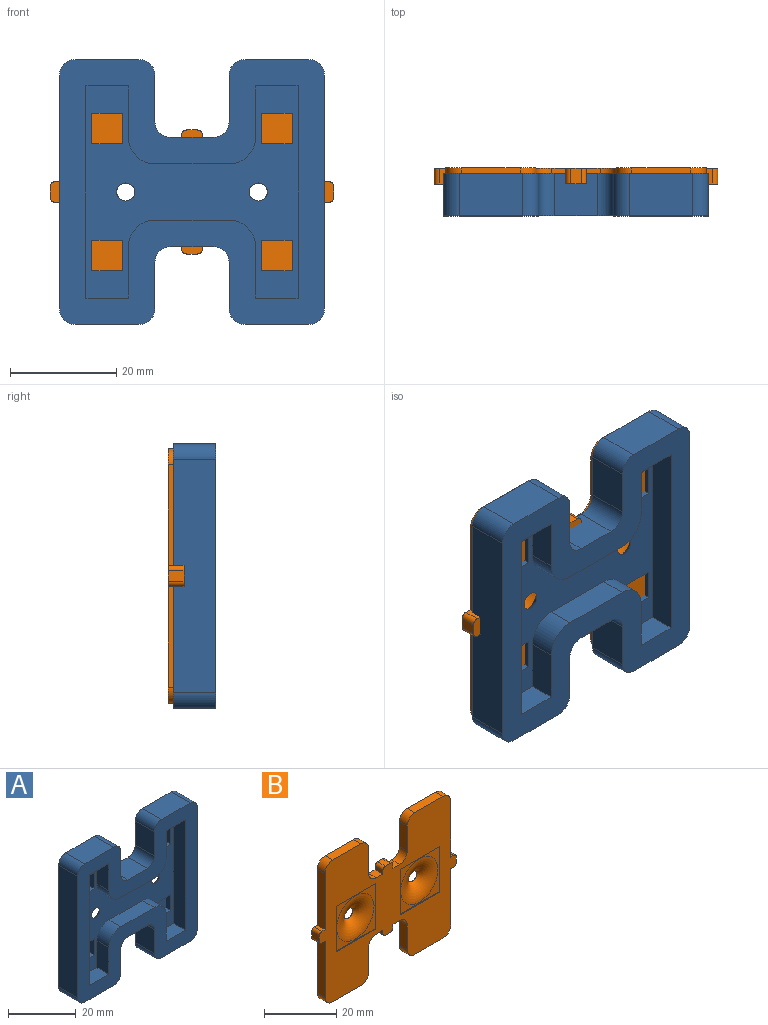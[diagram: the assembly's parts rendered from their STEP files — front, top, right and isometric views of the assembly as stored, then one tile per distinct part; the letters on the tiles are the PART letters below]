
ASSEMBLY  parts=2 mates=1
PART A: 75 faces, bbox 50x8x50 mm
  f0: plane 40x40mm, normal (0,-1,0), area 763.1mm2, adj f14,f15,f16,f17,f18,f19,f20,f21
  f1: plane 50x50mm, normal (0,1,0), area 1606.4mm2, adj f2,f3,f4,f5,f6,f7,f8,f9
  f2: plane 8x8mm, normal (0,0,-1), area 64mm2, adj f1,f26,f32,f33
  f3: plane 8.7x8mm, normal (-1,0,0), area 69.6mm2, adj f1,f26,f33,f34
  f4: plane 12x8mm, normal (0,0,-1), area 96mm2, adj f1,f26,f34,f35
  f5: plane 44x8mm, normal (1,0,0), area 352mm2, adj f1,f26,f35,f36
  f6: plane 12x8mm, normal (0,0,1), area 96mm2, adj f1,f26,f36,f37
  f7: plane 8.7x8mm, normal (-1,0,0), area 69.6mm2, adj f1,f26,f37,f38
  f8: plane 8x8mm, normal (0,0,1), area 64mm2, adj f1,f26,f27,f38
  f9: plane 8.7x8mm, normal (1,0,0), area 69.6mm2, adj f1,f26,f27,f28
  f10: plane 12x8mm, normal (0,0,1), area 96mm2, adj f1,f26,f28,f29
  f11: plane 44x8mm, normal (-1,0,0), area 352mm2, adj f1,f26,f29,f30
  f12: plane 12x8mm, normal (0,0,-1), area 96mm2, adj f1,f26,f30,f31
  f13: plane 8.7x8mm, normal (1,0,0), area 69.6mm2, adj f1,f26,f31,f32
  f14: plane 40x5mm, normal (1,0,0), area 200mm2, adj f0,f15,f25,f26
  f15: plane 8x5mm, normal (0,0,-1), area 40mm2, adj f0,f14,f16,f26
  f16: plane 9.7x5mm, normal (-1,0,0), area 48.5mm2, adj f0,f15,f26,f49
  f17: plane 14x5mm, normal (0,0,-1), area 70mm2, adj f0,f26,f49,f50
  f18: plane 9.7x5mm, normal (1,0,0), area 48.5mm2, adj f0,f19,f26,f50
  f19: plane 8x5mm, normal (0,0,-1), area 40mm2, adj f0,f18,f20,f26
  f20: plane 40x5mm, normal (-1,0,0), area 200mm2, adj f0,f19,f21,f26
  f21: plane 8x5mm, normal (0,0,1), area 40mm2, adj f0,f20,f22,f26
  f22: plane 9.7x5mm, normal (1,0,0), area 48.5mm2, adj f0,f21,f26,f51
  f23: plane 14x5mm, normal (0,0,1), area 70mm2, adj f0,f26,f51,f52
  f24: plane 9.7x5mm, normal (-1,0,0), area 48.5mm2, adj f0,f25,f26,f52
  f25: plane 8x5mm, normal (0,0,1), area 40mm2, adj f0,f14,f24,f26
  f26: plane 50x50mm, normal (0,-1,0), area 1164.8mm2, adj f2,f3,f4,f5,f6,f7,f8,f9
  f27: cylinder r=3mm len=8mm, axis (0,-1,0), area 37.7mm2, adj f1,f8,f9,f26
  f28: cylinder r=3mm len=8mm, axis (0,1,0), area 37.7mm2, adj f1,f9,f10,f26
  f29: cylinder r=3mm len=8mm, axis (0,1,0), area 37.7mm2, adj f1,f10,f11,f26
  f30: cylinder r=3mm len=8mm, axis (0,1,0), area 37.7mm2, adj f1,f11,f12,f26
  f31: cylinder r=3mm len=8mm, axis (0,1,0), area 37.7mm2, adj f1,f12,f13,f26
  f32: cylinder r=3mm len=8mm, axis (0,-1,0), area 37.7mm2, adj f1,f2,f13,f26
  f33: cylinder r=3mm len=8mm, axis (0,-1,0), area 37.7mm2, adj f1,f2,f3,f26
  f34: cylinder r=3mm len=8mm, axis (0,1,0), area 37.7mm2, adj f1,f3,f4,f26
  f35: cylinder r=3mm len=8mm, axis (0,1,0), area 37.7mm2, adj f1,f4,f5,f26
  f36: cylinder r=3mm len=8mm, axis (0,1,0), area 37.7mm2, adj f1,f5,f6,f26
  f37: cylinder r=3mm len=8mm, axis (0,1,0), area 37.7mm2, adj f1,f6,f7,f26
  f38: cylinder r=3mm len=8mm, axis (0,-1,0), area 37.7mm2, adj f1,f7,f8,f26
  f39: plane 15.4x0.1mm, normal (0,0,-1), area 1.5mm2, adj f1,f40,f42,f43
  f40: plane 15.4x0.1mm, normal (-1,0,0), area 1.5mm2, adj f1,f39,f41,f43
  f41: plane 15.4x0.1mm, normal (0,0,1), area 1.5mm2, adj f1,f40,f42,f43
  f42: plane 15.4x0.1mm, normal (1,0,0), area 1.5mm2, adj f1,f39,f41,f43
  f43: plane 15.4x15.4mm, normal (0,1,0), area 66.4mm2, adj f39,f40,f41,f42,f73
  f44: plane 15.4x0.1mm, normal (0,0,-1), area 1.5mm2, adj f1,f45,f47,f48
  f45: plane 15.4x0.1mm, normal (-1,0,0), area 1.5mm2, adj f1,f44,f46,f48
  f46: plane 15.4x0.1mm, normal (0,0,1), area 1.5mm2, adj f1,f45,f47,f48
  f47: plane 15.4x0.1mm, normal (1,0,0), area 1.5mm2, adj f1,f44,f46,f48
  f48: plane 15.4x15.4mm, normal (0,1,0), area 66.4mm2, adj f44,f45,f46,f47,f74
  f49: cylinder r=5mm len=5mm, axis (0,1,0), area 39.3mm2, adj f0,f16,f17,f26
  f50: cylinder r=5mm len=5mm, axis (0,1,0), area 39.3mm2, adj f0,f17,f18,f26
  f51: cylinder r=5mm len=5mm, axis (0,1,0), area 39.3mm2, adj f0,f22,f23,f26
  f52: cylinder r=5mm len=5mm, axis (0,1,0), area 39.3mm2, adj f0,f23,f24,f26
  f53: plane 5.8x2mm, normal (1,0,0), area 11.6mm2, adj f0,f54,f56,f57
  f54: plane 5.8x2mm, normal (0,0,1), area 11.6mm2, adj f0,f53,f55,f57
  f55: plane 5.8x2mm, normal (-1,0,0), area 11.6mm2, adj f0,f54,f56,f57
  f56: plane 5.8x2mm, normal (0,0,-1), area 11.6mm2, adj f0,f53,f55,f57
  f57: plane 5.8x5.8mm, normal (0,-1,0), area 33.6mm2, adj f53,f54,f55,f56
  f58: plane 5.8x2mm, normal (-1,0,0), area 11.6mm2, adj f0,f59,f61,f62
  f59: plane 5.8x2mm, normal (0,0,-1), area 11.6mm2, adj f0,f58,f60,f62
  f60: plane 5.8x2mm, normal (1,0,0), area 11.6mm2, adj f0,f59,f61,f62
  f61: plane 5.8x2mm, normal (0,0,1), area 11.6mm2, adj f0,f58,f60,f62
  f62: plane 5.8x5.8mm, normal (0,-1,0), area 33.6mm2, adj f58,f59,f60,f61
  f63: plane 5.8x2mm, normal (1,0,0), area 11.6mm2, adj f0,f64,f66,f67
  f64: plane 5.8x2mm, normal (0,0,1), area 11.6mm2, adj f0,f63,f65,f67
  f65: plane 5.8x2mm, normal (-1,0,0), area 11.6mm2, adj f0,f64,f66,f67
  f66: plane 5.8x2mm, normal (0,0,-1), area 11.6mm2, adj f0,f63,f65,f67
  f67: plane 5.8x5.8mm, normal (0,-1,0), area 33.6mm2, adj f63,f64,f65,f66
  f68: plane 5.8x2mm, normal (0,0,-1), area 11.6mm2, adj f0,f69,f71,f72
  f69: plane 5.8x2mm, normal (1,0,0), area 11.6mm2, adj f0,f68,f70,f72
  f70: plane 5.8x2mm, normal (0,0,1), area 11.6mm2, adj f0,f69,f71,f72
  f71: plane 5.8x2mm, normal (-1,0,0), area 11.6mm2, adj f0,f68,f70,f72
  f72: plane 5.8x5.8mm, normal (0,-1,0), area 33.6mm2, adj f68,f69,f70,f71
  f73: torus R=7.37mm, axis (0,1,0), area 178.9mm2, adj f0,f43
  f74: torus R=7.37mm, axis (0,1,0), area 178.9mm2, adj f0,f48
PART B: 82 faces, bbox 53.5x7.2x48 mm
  f0: plane 53.5x48mm, normal (0,-1,0), area 1470.3mm2, adj f2,f3,f4,f5,f6,f7,f8,f9
  f1: plane 53.5x48mm, normal (0,1,0), area 1791.9mm2, adj f2,f3,f4,f5,f6,f7,f8,f9
  f2: plane 3x2.55mm, normal (0,0,-1), area 7.7mm2, adj f0,f1,f3,f35
  f3: plane 3x1.2mm, normal (-1,0,0), area 3.6mm2, adj f0,f1,f2,f76
  f4: plane 3x2mm, normal (0,0,-1), area 6mm2, adj f0,f1,f76,f77
  f5: plane 3x1.2mm, normal (1,0,0), area 3.6mm2, adj f0,f1,f6,f77
  f6: plane 3x2.55mm, normal (0,0,-1), area 7.6mm2, adj f0,f1,f5,f36
  f7: plane 8.5x3mm, normal (-1,0,0), area 25.5mm2, adj f0,f1,f36,f37
  f8: plane 11x3mm, normal (0,0,-1), area 33mm2, adj f0,f1,f37,f38
  f9: plane 19x3mm, normal (1,0,0), area 57mm2, adj f0,f1,f10,f38
  f10: plane 3x1.2mm, normal (0,0,-1), area 3.6mm2, adj f0,f1,f9,f74
  f11: plane 3x2mm, normal (1,0,0), area 6mm2, adj f0,f1,f74,f75
  f12: plane 3x1.2mm, normal (0,0,1), area 3.6mm2, adj f0,f1,f13,f75
  f13: plane 19x3mm, normal (1,0,0), area 57mm2, adj f0,f1,f12,f39
  f14: plane 11x3mm, normal (0,0,1), area 33mm2, adj f0,f1,f39,f40
  f15: plane 8.5x3mm, normal (-1,0,0), area 25.5mm2, adj f0,f1,f40,f41
  f16: plane 3x2.55mm, normal (0,0,1), area 7.6mm2, adj f0,f1,f17,f41
  f17: plane 3x1.2mm, normal (1,0,0), area 3.6mm2, adj f0,f1,f16,f80
  f18: plane 3x2mm, normal (0,0,1), area 6mm2, adj f0,f1,f80,f81
  f19: plane 3x1.2mm, normal (-1,0,0), area 3.6mm2, adj f0,f1,f20,f81
  f20: plane 3x2.55mm, normal (0,0,1), area 7.7mm2, adj f0,f1,f19,f30
  f21: plane 8.5x3mm, normal (1,0,0), area 25.5mm2, adj f0,f1,f30,f31
  f22: plane 11x3mm, normal (0,0,1), area 33mm2, adj f0,f1,f31,f32
  f23: plane 19x3mm, normal (-1,0,0), area 57mm2, adj f0,f1,f24,f32
  f24: plane 3x1.2mm, normal (0,0,1), area 3.6mm2, adj f0,f1,f23,f78
  f25: plane 3x2mm, normal (-1,0,0), area 6mm2, adj f0,f1,f78,f79
  f26: plane 3x1.2mm, normal (0,0,-1), area 3.6mm2, adj f0,f1,f27,f79
  f27: plane 19x3mm, normal (-1,0,0), area 57mm2, adj f0,f1,f26,f33
  f28: plane 11x3mm, normal (0,0,-1), area 33mm2, adj f0,f1,f33,f34
  f29: plane 8.5x3mm, normal (1,0,0), area 25.5mm2, adj f0,f1,f34,f35
  f30: cylinder r=3mm len=3mm, axis (0,-1,0), area 14.1mm2, adj f0,f1,f20,f21
  f31: cylinder r=3mm len=3mm, axis (0,1,0), area 14.1mm2, adj f0,f1,f21,f22
  f32: cylinder r=3mm len=3mm, axis (0,1,0), area 14.1mm2, adj f0,f1,f22,f23
  f33: cylinder r=3mm len=3mm, axis (0,1,0), area 14.1mm2, adj f0,f1,f27,f28
  f34: cylinder r=3mm len=3mm, axis (0,1,0), area 14.1mm2, adj f0,f1,f28,f29
  f35: cylinder r=3mm len=3mm, axis (0,-1,0), area 14.1mm2, adj f0,f1,f2,f29
  f36: cylinder r=3mm len=3mm, axis (0,-1,0), area 14.1mm2, adj f0,f1,f6,f7
  f37: cylinder r=3mm len=3mm, axis (0,1,0), area 14.1mm2, adj f0,f1,f7,f8
  f38: cylinder r=3mm len=3mm, axis (0,1,0), area 14.1mm2, adj f0,f1,f8,f9
  f39: cylinder r=3mm len=3mm, axis (0,1,0), area 14.1mm2, adj f0,f1,f13,f14
  f40: cylinder r=3mm len=3mm, axis (0,1,0), area 14.1mm2, adj f0,f1,f14,f15
  f41: cylinder r=3mm len=3mm, axis (0,-1,0), area 14.1mm2, adj f0,f1,f15,f16
  f42: plane 5.8x2mm, normal (0,0,-1), area 11.6mm2, adj f1,f43,f45,f46
  f43: plane 5.8x2mm, normal (-1,0,0), area 11.6mm2, adj f1,f42,f44,f46
  f44: plane 5.8x2mm, normal (0,0,1), area 11.6mm2, adj f1,f43,f45,f46
  f45: plane 5.8x2mm, normal (1,0,0), area 11.6mm2, adj f1,f42,f44,f46
  f46: plane 5.8x5.8mm, normal (0,1,0), area 33.6mm2, adj f42,f43,f44,f45
  f47: plane 5.8x2mm, normal (0,0,1), area 11.6mm2, adj f1,f48,f50,f51
  f48: plane 5.8x2mm, normal (1,0,0), area 11.6mm2, adj f1,f47,f49,f51
  f49: plane 5.8x2mm, normal (0,0,-1), area 11.6mm2, adj f1,f48,f50,f51
  f50: plane 5.8x2mm, normal (-1,0,0), area 11.6mm2, adj f1,f47,f49,f51
  f51: plane 5.8x5.8mm, normal (0,1,0), area 33.6mm2, adj f47,f48,f49,f50
  f52: plane 5.8x2mm, normal (0,0,1), area 11.6mm2, adj f1,f53,f55,f56
  f53: plane 5.8x2mm, normal (1,0,0), area 11.6mm2, adj f1,f52,f54,f56
  f54: plane 5.8x2mm, normal (0,0,-1), area 11.6mm2, adj f1,f53,f55,f56
  f55: plane 5.8x2mm, normal (-1,0,0), area 11.6mm2, adj f1,f52,f54,f56
  f56: plane 5.8x5.8mm, normal (0,1,0), area 33.6mm2, adj f52,f53,f54,f55
  f57: plane 5.8x2mm, normal (-1,0,0), area 11.6mm2, adj f1,f58,f60,f61
  f58: plane 5.8x2mm, normal (0,0,1), area 11.6mm2, adj f1,f57,f59,f61
  f59: plane 5.8x2mm, normal (1,0,0), area 11.6mm2, adj f1,f58,f60,f61
  f60: plane 5.8x2mm, normal (0,0,-1), area 11.6mm2, adj f1,f57,f59,f61
  f61: plane 5.8x5.8mm, normal (0,1,0), area 33.6mm2, adj f57,f58,f59,f60
  f62: plane 15.4x0.2mm, normal (0,0,-1), area 3.1mm2, adj f0,f63,f65,f66
  f63: plane 15.4x0.2mm, normal (1,0,0), area 3.1mm2, adj f0,f62,f64,f66
  f64: plane 15.4x0.2mm, normal (0,0,1), area 3.1mm2, adj f0,f63,f65,f66
  f65: plane 15.4x0.2mm, normal (-1,0,0), area 3.1mm2, adj f0,f62,f64,f66
  f66: plane 15.4x15.4mm, normal (0,-1,0), area 69.7mm2, adj f62,f63,f64,f65,f73
  f67: plane 15.4x0.2mm, normal (0,0,-1), area 3.1mm2, adj f0,f68,f70,f71
  f68: plane 15.4x0.2mm, normal (1,0,0), area 3.1mm2, adj f0,f67,f69,f71
  f69: plane 15.4x0.2mm, normal (0,0,1), area 3.1mm2, adj f0,f68,f70,f71
  f70: plane 15.4x0.2mm, normal (-1,0,0), area 3.1mm2, adj f0,f67,f69,f71
  f71: plane 15.4x15.4mm, normal (0,-1,0), area 69.7mm2, adj f67,f68,f69,f70,f72
  f72: torus R=7.3mm, axis (0,-1,0), area 174.6mm2, adj f1,f71
  f73: torus R=7.3mm, axis (0,-1,0), area 174.6mm2, adj f1,f66
  f74: cylinder r=1mm len=3mm, axis (0,1,0), area 4.7mm2, adj f0,f1,f10,f11
  f75: cylinder r=1mm len=3mm, axis (0,-1,0), area 4.7mm2, adj f0,f1,f11,f12
  f76: cylinder r=1mm len=3mm, axis (0,1,0), area 4.7mm2, adj f0,f1,f3,f4
  f77: cylinder r=1mm len=3mm, axis (0,-1,0), area 4.7mm2, adj f0,f1,f4,f5
  f78: cylinder r=1mm len=3mm, axis (0,-1,0), area 4.7mm2, adj f0,f1,f24,f25
  f79: cylinder r=1mm len=3mm, axis (0,1,0), area 4.7mm2, adj f0,f1,f25,f26
  f80: cylinder r=1mm len=3mm, axis (0,1,0), area 4.7mm2, adj f0,f1,f17,f18
  f81: cylinder r=1mm len=3mm, axis (0,-1,0), area 4.7mm2, adj f0,f1,f18,f19
PLACE A t=(26.95,13.69,-24.37)mm
PLACE B t=(7.5,14.69,-14.17)mm
MATE fastened A.f67 <-> B.f51  axis (0,-1,0) through (31.74,12.69,10.62)mm
